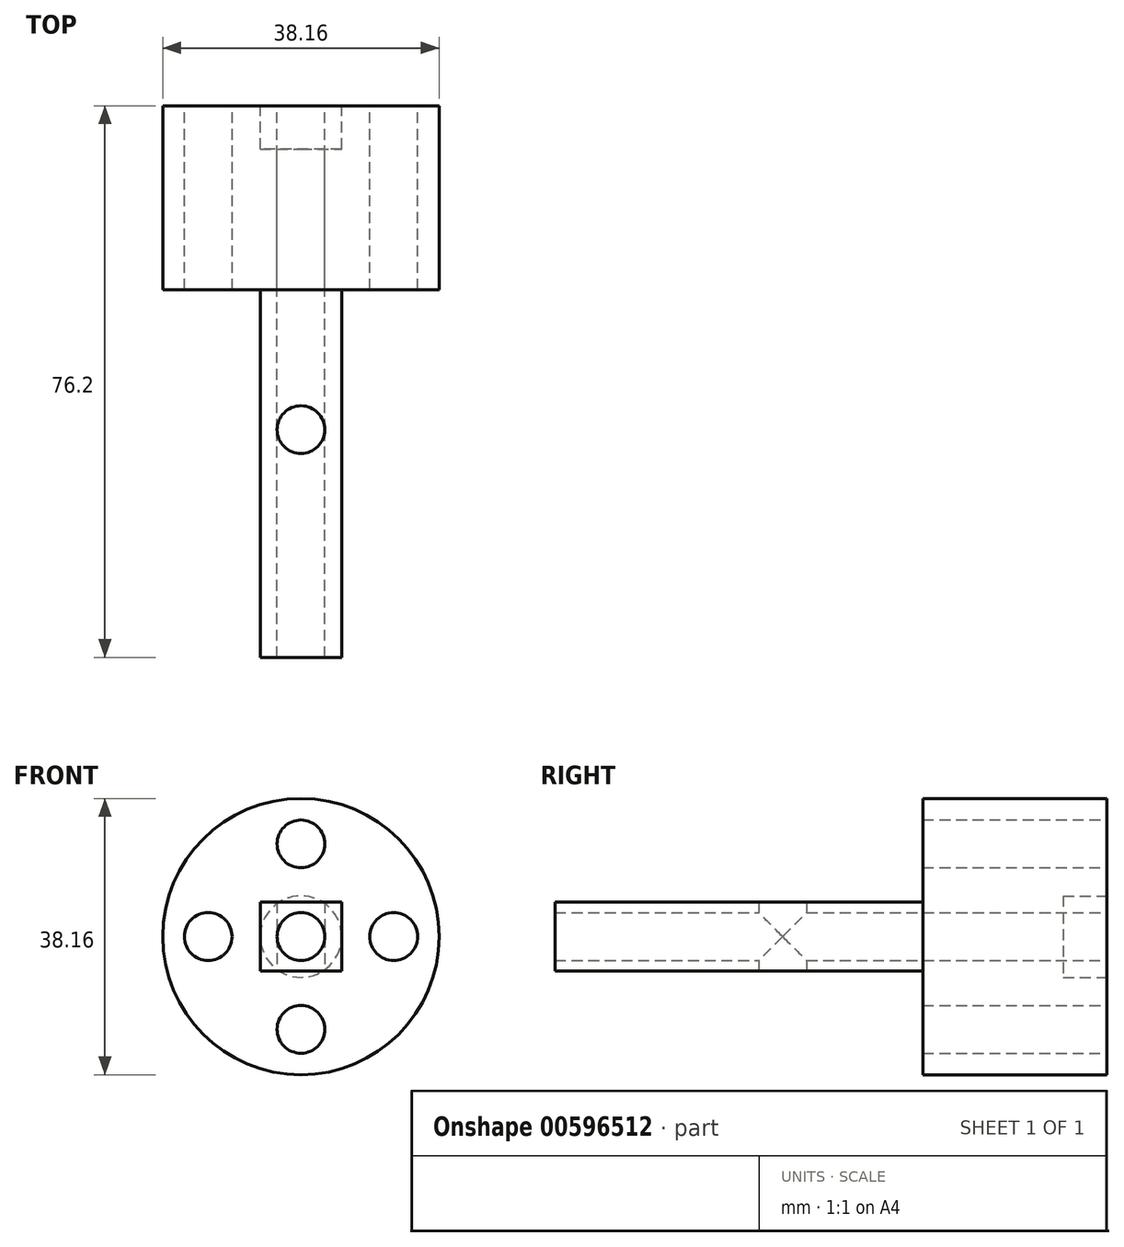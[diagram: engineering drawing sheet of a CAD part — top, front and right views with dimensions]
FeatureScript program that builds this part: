
annotation { "Feature Type Name" : "Feature", "Feature Type Description" : "" }
export const myFeature = defineFeature(function(context is Context, id is Id, definition is map)
    precondition{}
    {
        {
            var Q0;
            Q0=qCreatedBy(makeId("Front.planeOp"),FACE);
            var sketch = newSketch(context, id + "F0", { "sketchPlane" : qUnion([Q0])});
            skCircle(sketch, "E0", {"center": v(0, 0) * mm, "radius": 19.08 * mm});
            skPoint(sketch, "E1", {"position": v(-12.8, 0) * mm});
            skPoint(sketch, "E2.1.0", {"position": v(0, -12.8) * mm});
            skPoint(sketch, "E2.2.0", {"position": v(12.8, 0) * mm});
            skPoint(sketch, "E2.3.0", {"position": v(0, 12.8) * mm});
            skSolve(sketch);
        }
        {
            var Q0;
            Q0=makeQuery(id+"F0.imprint","IMPRINT",FACE,{"disambiguationData":[TD([[makeQuery(id+"F0.imprint","IMPRINT",EDGE,{"derivedFrom":sQuery(id+"F0.wireOp",EDGE,"E0")}),1.0]])]});
            extrude(context, id + "F1", {"entities" : qUnion([Q0]), "depth" : 25.4 * mm, "offsetDistance" : 25.4 * mm});
        }
        {
            var Q0;
            Q0=sQuery(id+"F0.wireOp",VERTEX,"E2.3.0");
            var Q1;
            Q1=sQuery(id+"F0.wireOp",VERTEX,"E2.2.0");
            var Q2;
            Q2=sQuery(id+"F0.wireOp",VERTEX,"E2.1.0");
            var Q3;
            Q3=sQuery(id+"F0.wireOp",VERTEX,"E1");
            var Q4;
            Q4=makeQuery(id+"F1.opExtrude","SWEPT_BODY",BODY,{"disambiguationData":[OSD([sQuery(id+"F0.wireOp",EDGE,"E0")])]});
            hole(context, id + "F2", {"style" : HoleStyle.SIMPLE, "endStyle" : HoleEndStyle.THROUGH, "oppositeDirection" : true, "standardTappedOrClearance" : lookupTablePath({ "standard" : "ISO", "fit" : "Normal", "size" : "M6", "type" : "Clearance" }), "standardBlindInLast" : lookupTablePath({ "fit" : "Standard", "standard" : "ISO", "size" : "M6", "type" : "Clearance" }), "holeDiameter" : 6.6 * mm, "majorDiameter" : 6.35 * mm, "isTappedThrough" : true, "tappedDepth" : 12.7 * mm, "tapClearance" : 3, "startFromSketch" : true, "locations" : qUnion([Q0, Q1, Q2, Q3]), "scope" : qUnion([Q4])});
        }
        {
            var Q0;
            Q0=makeQuery(id+"F1.opExtrude","CAP_FACE",FACE,{"disambiguationData":[OSD([sQuery(id+"F0.wireOp",EDGE,"E0")])],"isStart":false});
            var sketch = newSketch(context, id + "F3", { "sketchPlane" : qUnion([Q0])});
            skLineSegment(sketch, "E3.bottom", {"start": v(5.61, 4.75) * mm, "end": v(-5.61, 4.75) * mm});
            skLineSegment(sketch, "E3.top", {"start": v(5.61, -4.75) * mm, "end": v(-5.61, -4.75) * mm});
            skLineSegment(sketch, "E3.left", {"start": v(5.61, 4.75) * mm, "end": v(5.61, -4.75) * mm});
            skLineSegment(sketch, "E3.right", {"start": v(-5.61, 4.75) * mm, "end": v(-5.61, -4.75) * mm});
            skPoint(sketch, "E3.middle", {"position": v(0, 0) * mm});
            skSolve(sketch);
        }
        {
            var Q0;
            Q0=makeQuery(id+"F3.imprint","IMPRINT",FACE,{"disambiguationData":[TD([[makeQuery(id+"F3.imprint","IMPRINT",EDGE,{"derivedFrom":sQuery(id+"F3.wireOp",EDGE,"E3.bottom")}),1.0]])]});
            extrude(context, id + "F4", {"entities" : qUnion([Q0]), "operationType" : NewBodyOperationType.ADD, "depth" : 50.8 * mm, "offsetDistance" : 25.4 * mm});
        }
        {
            var Q0;
            Q0=makeQuery(id+"F4.opExtrude","SWEPT_FACE",FACE,{"disambiguationData":[OSD([sQuery(id+"F3.wireOp",EDGE,"E3.top")])]});
            var sketch = newSketch(context, id + "F5", { "sketchPlane" : qUnion([Q0])});
            skCircle(sketch, "E4", {"center": v(0, 44.75) * mm, "radius": 2.6 * mm});
            skSolve(sketch);
        }
        {
            var Q0;
            Q0=sQuery(id+"F5.wireOp",VERTEX,"E4.center");
            var Q1;
            Q1=makeQuery(id+"F1.opExtrude","SWEPT_BODY",BODY,{"disambiguationData":[OSD([sQuery(id+"F0.wireOp",EDGE,"E0")])]});
            hole(context, id + "F6", {"style" : HoleStyle.SIMPLE, "endStyle" : HoleEndStyle.THROUGH, "standardTappedOrClearance" : lookupTablePath({ "standard" : "ISO", "fit" : "Normal", "size" : "M6", "type" : "Clearance" }), "standardBlindInLast" : lookupTablePath({ "fit" : "Standard", "standard" : "ISO", "size" : "M6", "type" : "Clearance" }), "holeDiameter" : 6.6 * mm, "majorDiameter" : 6.35 * mm, "isTappedThrough" : true, "tappedDepth" : 12.7 * mm, "tapClearance" : 3, "startFromSketch" : true, "locations" : qUnion([Q0]), "scope" : qUnion([Q1])});
        }
        {
            var Q0;
            Q0=sQuery(id+"F0.wireOp",VERTEX,"E0.center");
            var Q1;
            Q1=makeQuery(id+"F1.opExtrude","SWEPT_BODY",BODY,{"disambiguationData":[OSD([sQuery(id+"F0.wireOp",EDGE,"E0")])]});
            hole(context, id + "F7", {"style" : HoleStyle.C_BORE, "endStyle" : HoleEndStyle.THROUGH, "oppositeDirection" : true, "standardTappedOrClearance" : lookupTablePath({ "standard" : "ISO", "fit" : "Normal", "size" : "M6", "type" : "Clearance" }), "standardBlindInLast" : lookupTablePath({ "fit" : "Standard", "standard" : "ISO", "size" : "M6", "type" : "Clearance" }), "holeDiameter" : 6.6 * mm, "cBoreDiameter" : 11.25 * mm, "cBoreDepth" : 6 * mm, "majorDiameter" : 6.35 * mm, "isTappedThrough" : true, "tappedDepth" : 12.7 * mm, "tapClearance" : 3, "startFromSketch" : true, "locations" : qUnion([Q0]), "scope" : qUnion([Q1])});
        }
    });
